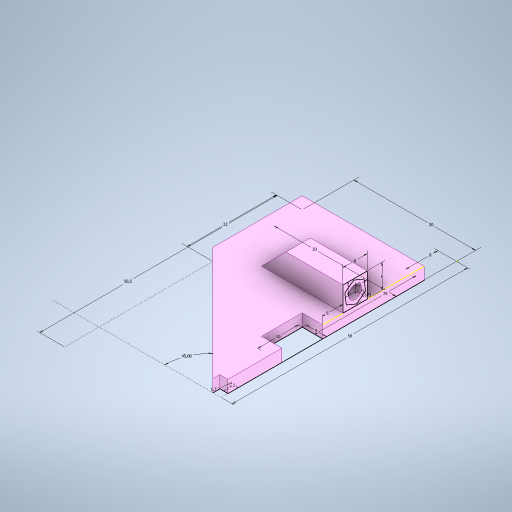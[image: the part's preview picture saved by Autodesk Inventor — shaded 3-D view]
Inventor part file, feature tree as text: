
AUTODESK INVENTOR PART (.ipt)
format: ipt  version: 2023 (Build 270158000, 158)  size: 319,488 bytes
history: native  units: in
note: dims shown in document units (in); Inventor stores cm internally (conversion verified against a paired STEP export)
features: extrude x4, sketch x2, other x1, chamfer x1, hole x1
ambient origin geometry x8: Origin, YZ Plane, XZ Plane, XY Plane, X Axis, Y Axis, Z Axis, Center Point
bodies: Body1 (feature_tree)
feature tree (9):
  other  "Bryła1"
  sketch  "Szkic1"
  extrude  "Wyciągnięcie proste1"  Depth=0.0787in
  extrude  "Wyciągnięcie proste2"  Depth=1.1811in
  sketch  "Sketch2"  dims[d0=2.2835in d1=0.0787in d2=0.0669in d4=45.0deg d5=0.1181in d6=0.0in d7=0.0787in d8=0.1969in d9=0.3937in d10=0.3937in d11=0.0in d13=1.1811in d14=0.8661in d15=2.3031in d16=1.1811in d17=0.9843in d18=0.315in d19=0.2362in d20=0.2362in d21=0.1969in d22=0.7874in d23=0.0in d24=0.1181in d25=0.1181in d29=0.0659in d30=0.1083in d31=0.2362in d32=0.0in d33=0.2362in d34=0.0787in d35=45.0deg d36=0.126in d37=0.2362in d38=0.1575in d39=0.0787in d40=90.0deg d41=1.1811in d42=0.0in]
  extrude  "Extrusion3"  TaperAngle=45.0deg  [1 undecoded]
  extrude  "Extrusion4"  Depth=0.1181in TaperAngle=0.0deg
  chamfer  "Chamfer2"  Distance=0.0787in
  hole  "Hole1"  [1 undecoded]
note: 2 required parameter values undecoded (feature->parameter linkage not recoverable at this tier; creation-order binding heuristic only, values carry confidence <= 0.55)
